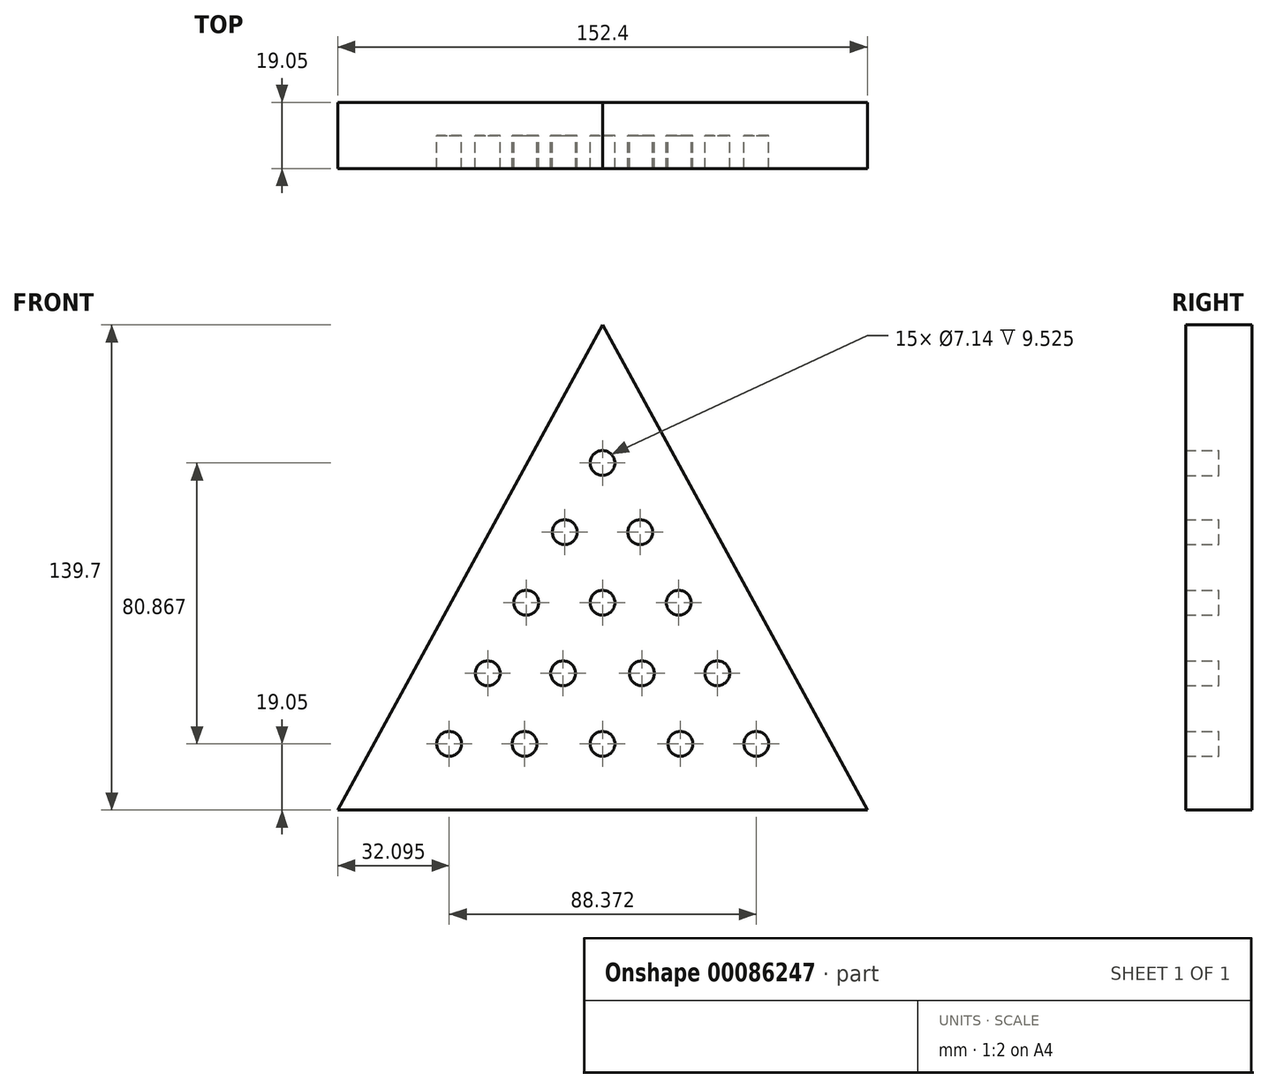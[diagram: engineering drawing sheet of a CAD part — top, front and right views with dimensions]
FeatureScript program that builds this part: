
annotation { "Feature Type Name" : "Feature", "Feature Type Description" : "" }
export const myFeature = defineFeature(function(context is Context, id is Id, definition is map)
    precondition{}
    {
        {
            var Q0;
            Q0=qCreatedBy(makeId("Front.planeOp"),FACE);
            var sketch = newSketch(context, id + "F0", { "sketchPlane" : qUnion([Q0])});
            skLineSegment(sketch, "E0.bottom", {"start": v(-80.66, 59.69) * mm, "end": v(71.74, 59.69) * mm});
            skLineSegment(sketch, "E0.top", {"start": v(-80.66, -80.01) * mm, "end": v(71.74, -80.01) * mm});
            skLineSegment(sketch, "E0.left", {"start": v(-80.66, 59.69) * mm, "end": v(-80.66, -80.01) * mm});
            skLineSegment(sketch, "E0.right", {"start": v(71.74, 59.7) * mm, "end": v(71.74, -80.01) * mm});
            skLineSegment(sketch, "E1", {"start": v(-80.66, -80.01) * mm, "end": v(-4.46, 59.69) * mm});
            skLineSegment(sketch, "E2", {"start": v(-4.46, 59.7) * mm, "end": v(71.74, -80.01) * mm});
            skCircle(sketch, "E3", {"center": v(-4.46, -60.96) * mm, "radius": 3.57 * mm});
            skCircle(sketch, "E4", {"center": v(-26.87, -60.96) * mm, "radius": 3.57 * mm});
            skCircle(sketch, "E5", {"center": v(-48.57, -60.96) * mm, "radius": 3.57 * mm});
            skCircle(sketch, "E6", {"center": v(17.95, -60.96) * mm, "radius": 3.57 * mm});
            skCircle(sketch, "E7", {"center": v(39.8, -60.96) * mm, "radius": 3.57 * mm});
            skCircle(sketch, "E8", {"center": v(-37.48, -40.64) * mm, "radius": 3.57 * mm});
            skCircle(sketch, "E9", {"center": v(-15.78, -40.64) * mm, "radius": 3.57 * mm});
            skCircle(sketch, "E10", {"center": v(6.87, -40.64) * mm, "radius": 3.57 * mm});
            skCircle(sketch, "E11", {"center": v(28.57, -40.64) * mm, "radius": 3.57 * mm});
            skCircle(sketch, "E12", {"center": v(17.49, -20.32) * mm, "radius": 3.57 * mm});
            skCircle(sketch, "E13", {"center": v(-4.46, -20.32) * mm, "radius": 3.57 * mm});
            skCircle(sketch, "E14", {"center": v(-26.4, -20.32) * mm, "radius": 3.57 * mm});
            skCircle(sketch, "E15", {"center": v(-15.31, 0) * mm, "radius": 3.57 * mm});
            skCircle(sketch, "E16", {"center": v(6.4, 0) * mm, "radius": 3.57 * mm});
            skCircle(sketch, "E17", {"center": v(-4.46, 19.9) * mm, "radius": 3.57 * mm});
            skSolve(sketch);
        }
        {
            var Q0;
            Q0=makeQuery(id+"F0.imprint","IMPRINT",FACE,{"disambiguationData":[TD([[makeQuery(id+"F0.imprint","IMPRINT",EDGE,{"derivedFrom":sQuery(id+"F0.wireOp",EDGE,"E0.top")}),1.0]])]});
            extrude(context, id + "F1", {"entities" : qUnion([Q0]), "depth" : 19.05 * mm});
        }
        {
            var Q0;
            Q0=makeQuery(id+"F0.imprint","IMPRINT",FACE,{"disambiguationData":[TD([[makeQuery(id+"F0.imprint","IMPRINT",EDGE,{"derivedFrom":sQuery(id+"F0.wireOp",EDGE,"E17")}),1.0]])]});
            var Q1;
            Q1=makeQuery(id+"F0.imprint","IMPRINT",FACE,{"disambiguationData":[TD([[makeQuery(id+"F0.imprint","IMPRINT",EDGE,{"derivedFrom":sQuery(id+"F0.wireOp",EDGE,"E15")}),1.0]])]});
            var Q2;
            Q2=makeQuery(id+"F0.imprint","IMPRINT",FACE,{"disambiguationData":[TD([[makeQuery(id+"F0.imprint","IMPRINT",EDGE,{"derivedFrom":sQuery(id+"F0.wireOp",EDGE,"E16")}),1.0]])]});
            var Q3;
            Q3=makeQuery(id+"F0.imprint","IMPRINT",FACE,{"disambiguationData":[TD([[makeQuery(id+"F0.imprint","IMPRINT",EDGE,{"derivedFrom":sQuery(id+"F0.wireOp",EDGE,"E12")}),1.0]])]});
            var Q4;
            Q4=makeQuery(id+"F0.imprint","IMPRINT",FACE,{"disambiguationData":[TD([[makeQuery(id+"F0.imprint","IMPRINT",EDGE,{"derivedFrom":sQuery(id+"F0.wireOp",EDGE,"E13")}),1.0]])]});
            var Q5;
            Q5=makeQuery(id+"F0.imprint","IMPRINT",FACE,{"disambiguationData":[TD([[makeQuery(id+"F0.imprint","IMPRINT",EDGE,{"derivedFrom":sQuery(id+"F0.wireOp",EDGE,"E14")}),1.0]])]});
            var Q6;
            Q6=makeQuery(id+"F0.imprint","IMPRINT",FACE,{"disambiguationData":[TD([[makeQuery(id+"F0.imprint","IMPRINT",EDGE,{"derivedFrom":sQuery(id+"F0.wireOp",EDGE,"E8")}),1.0]])]});
            var Q7;
            Q7=makeQuery(id+"F0.imprint","IMPRINT",FACE,{"disambiguationData":[TD([[makeQuery(id+"F0.imprint","IMPRINT",EDGE,{"derivedFrom":sQuery(id+"F0.wireOp",EDGE,"E9")}),1.0]])]});
            var Q8;
            Q8=makeQuery(id+"F0.imprint","IMPRINT",FACE,{"disambiguationData":[TD([[makeQuery(id+"F0.imprint","IMPRINT",EDGE,{"derivedFrom":sQuery(id+"F0.wireOp",EDGE,"E10")}),1.0]])]});
            var Q9;
            Q9=makeQuery(id+"F0.imprint","IMPRINT",FACE,{"disambiguationData":[TD([[makeQuery(id+"F0.imprint","IMPRINT",EDGE,{"derivedFrom":sQuery(id+"F0.wireOp",EDGE,"E11")}),1.0]])]});
            var Q10;
            Q10=makeQuery(id+"F0.imprint","IMPRINT",FACE,{"disambiguationData":[TD([[makeQuery(id+"F0.imprint","IMPRINT",EDGE,{"derivedFrom":sQuery(id+"F0.wireOp",EDGE,"E7")}),1.0]])]});
            var Q11;
            Q11=makeQuery(id+"F0.imprint","IMPRINT",FACE,{"disambiguationData":[TD([[makeQuery(id+"F0.imprint","IMPRINT",EDGE,{"derivedFrom":sQuery(id+"F0.wireOp",EDGE,"E6")}),1.0]])]});
            var Q12;
            Q12=makeQuery(id+"F0.imprint","IMPRINT",FACE,{"disambiguationData":[TD([[makeQuery(id+"F0.imprint","IMPRINT",EDGE,{"derivedFrom":sQuery(id+"F0.wireOp",EDGE,"E3")}),1.0]])]});
            var Q13;
            Q13=makeQuery(id+"F0.imprint","IMPRINT",FACE,{"disambiguationData":[TD([[makeQuery(id+"F0.imprint","IMPRINT",EDGE,{"derivedFrom":sQuery(id+"F0.wireOp",EDGE,"E4")}),1.0]])]});
            var Q14;
            Q14=makeQuery(id+"F0.imprint","IMPRINT",FACE,{"disambiguationData":[TD([[makeQuery(id+"F0.imprint","IMPRINT",EDGE,{"derivedFrom":sQuery(id+"F0.wireOp",EDGE,"E5")}),1.0]])]});
            extrude(context, id + "F2", {"entities" : qUnion([Q0, Q1, Q2, Q3, Q4, Q5, Q6, Q7, Q8, Q9, Q10, Q11, Q12, Q13, Q14]), "operationType" : NewBodyOperationType.ADD, "flatOperationType" : FlatOperationType.REMOVE, "offsetDistance" : 25.4 * mm, "depth" : 9.52 * mm, "domain" : OperationDomain.MODEL});
        }
    });
